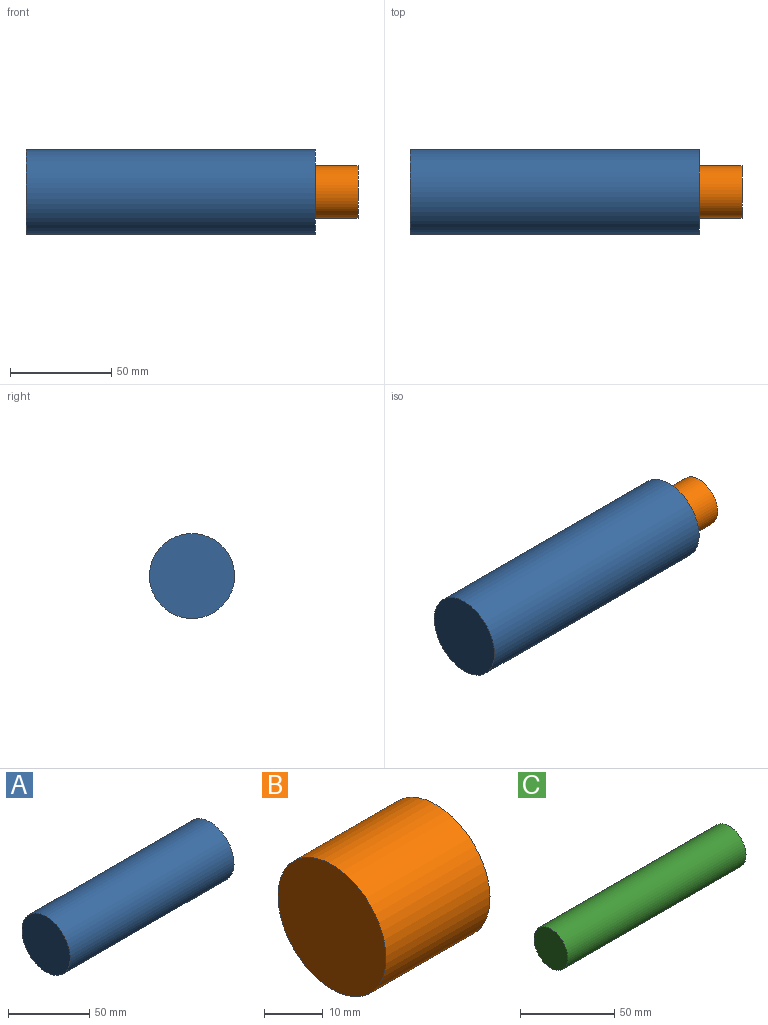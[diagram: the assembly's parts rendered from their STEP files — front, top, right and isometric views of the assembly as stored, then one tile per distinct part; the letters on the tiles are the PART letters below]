
ASSEMBLY  parts=3 mates=4
PART A: 11 faces, bbox 143x42x42 mm
  f0: plane 26x26mm, normal (1,0,0), area 530.9mm2, adj f1
  f1: cylinder r=13mm len=70mm, axis (-1,0,0), area 5717.7mm2, adj f0,f2
  f2: cone r=15.86mm half-angle=31deg, axis (1,0,0), area 503.5mm2, adj f1,f3
  f3: torus R=15mm, axis (-1,0,0), area 54.2mm2, adj f2,f4
  f4: cylinder r=16mm len=32mm, axis (-1,0,0), area 2284.4mm2, adj f3,f5
  f5: plane 32x32mm, normal (-1,0,0), area 188.5mm2, adj f4,f6
  f6: torus R=14mm, axis (-1,0,0), area 131.9mm2, adj f5,f7
  f7: cylinder r=13mm len=39mm, axis (-1,0,0), area 3185.6mm2, adj f6,f8
  f8: plane 42x42mm, normal (1,0,0), area 854.5mm2, adj f7,f9
  f9: cylinder r=21mm len=143mm, axis (-1,0,0), area 18868.4mm2, adj f8,f10
  f10: plane 42x42mm, normal (-1,0,0), area 1385.4mm2, adj f9
PART B: 3 faces, bbox 25x26x26 mm
  f0: plane 25.95x25.95mm, normal (-1,0,0), area 528.9mm2, adj f2
  f1: plane 25.95x25.95mm, normal (1,0,0), area 528.9mm2, adj f2
  f2: cylinder r=12.97mm len=25.95mm, axis (1,0,0), area 2038.1mm2, adj f0,f1
PART C: 3 faces, bbox 134x25.4x25.4 mm
  f0: plane 25.4x25.4mm, normal (-1,0,0), area 506.7mm2, adj f2
  f1: plane 25.4x25.4mm, normal (1,0,0), area 506.7mm2, adj f2
  f2: cylinder r=12.7mm len=134mm, axis (1,0,0), area 10692.7mm2, adj f0,f1
PLACE A t=(10.92,32.31,-16.41)mm
PLACE B t=(144.92,32.31,-16.41)mm
PLACE C t=(10.92,32.31,-16.41)mm
MATE cylindrical C.f2 <-> A.f1  axis (1,0,0) through (77.92,32.31,-16.41)mm
MATE planar C.f2 <-> A.f1  axis (-1,0,0) through (10.92,32.31,-16.41)mm
MATE planar B.f2 <-> C.f2  axis (-1,0,0) through (144.92,32.31,-16.41)mm
MATE cylindrical B.f2 <-> A.f1  axis (-1,0,0) through (144.92,32.31,-16.41)mm
